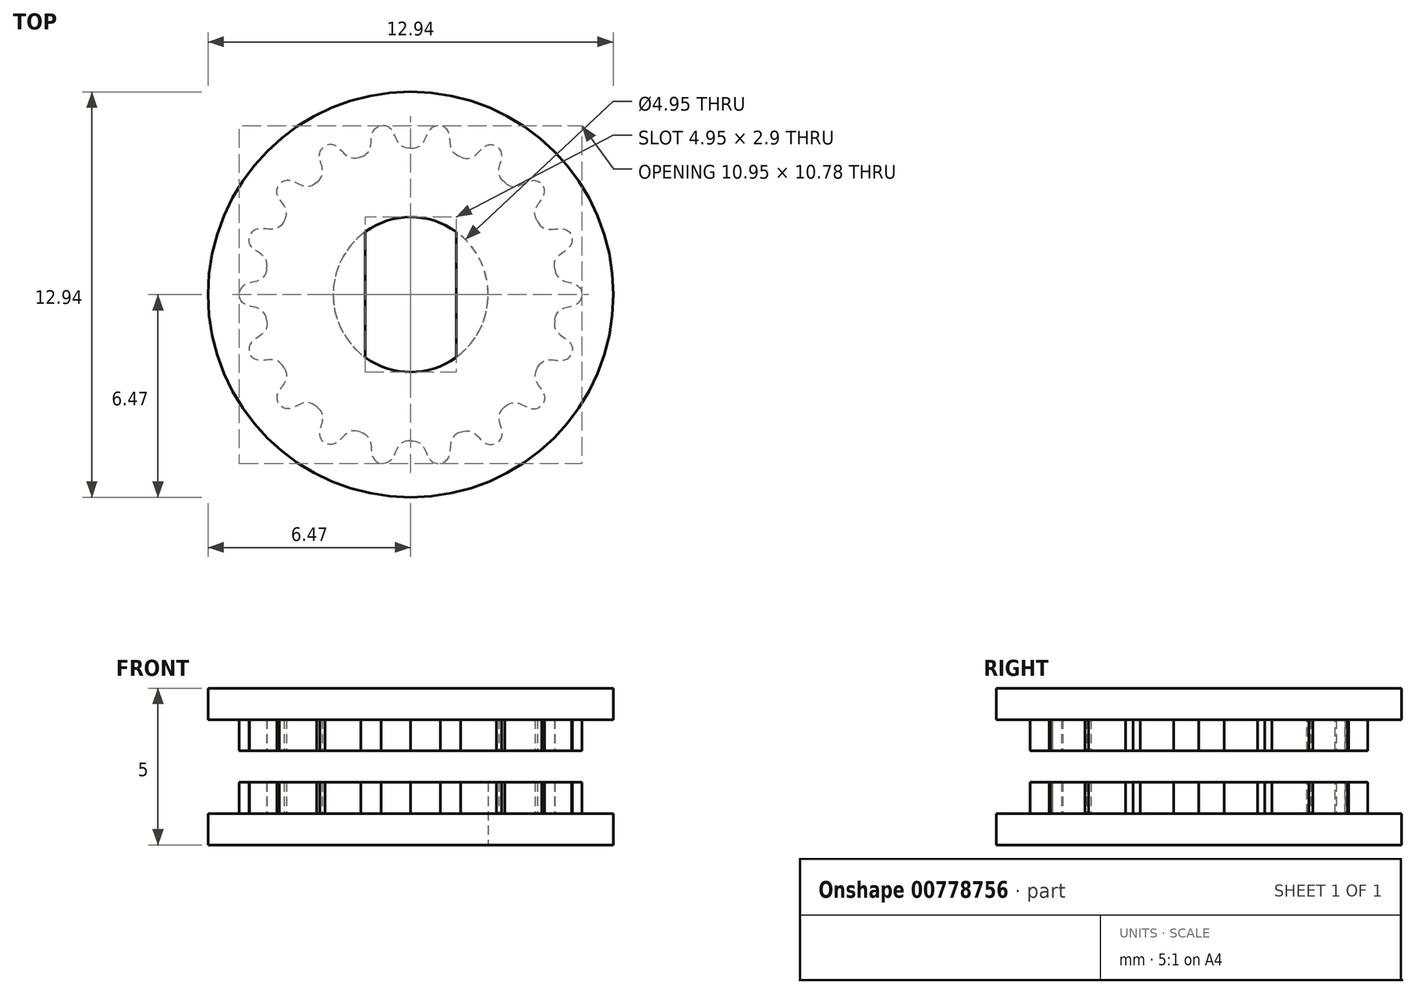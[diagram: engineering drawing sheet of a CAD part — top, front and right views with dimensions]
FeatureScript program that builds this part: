
annotation { "Feature Type Name" : "Feature", "Feature Type Description" : "" }
export const myFeature = defineFeature(function(context is Context, id is Id, definition is map)
    precondition{}
    {
        {
            assignVariable(context, id + "F0", {"name" : "teeth", "anyValue" : 18});
        }
        {
            var Q0;
            Q0=qCreatedBy(makeId("Top.planeOp"),FACE);
            var sketch = newSketch(context, id + "F1", { "sketchPlane" : qUnion([Q0])});
            skCircle(sketch, "E0", {"center": v(0, 0) * mm, "radius": 5.47 * mm, "construction": true});
            skLineSegment(sketch, "E1", {"start": v(0, 0) * mm, "end": v(0, 5.47) * mm, "construction": true});
            skLineSegment(sketch, "E2", {"start": v(0, 0) * mm, "end": v(0.95, 5.4) * mm, "construction": true});
            skArc(sketch, "E3", {"start": v(0.81, 4.6) * mm, "mid": v(0.4, 4.66) * mm, "end": v(0, 4.67) * mm, "construction": true});
            skLineSegment(sketch, "E4", {"start": v(0.61, 5.44) * mm, "end": v(0, 1.98) * mm, "construction": true});
            skFitSpline(sketch, "E5", {"points": [v(0, 4.67) * mm, v(0.57, 5.2) * mm, v(0.95, 5.4) * mm], "startDerivative": vector(2.16, -0.1) * mm, "endDerivative": vector(1.18, -0.19) * mm});
            skFitSpline(sketch, "E6.MirrorCS", {"points": [v(0, 4.67) * mm, v(-0.57, 5.2) * mm, v(-0.95, 5.4) * mm], "startDerivative": vector(-2.16, -0.1) * mm, "endDerivative": vector(-1.18, -0.19) * mm});
            skArc(sketch, "E7", {"start": v(0.95, 5.4) * mm, "mid": v(0, 5.47) * mm, "end": v(-0.95, 5.4) * mm});
            skLineSegment(sketch, "E8", {"start": v(-0.95, 5.4) * mm, "end": v(-1.12, 6.37) * mm});
            skArc(sketch, "E9", {"start": v(1.12, 6.37) * mm, "mid": v(0, 6.47) * mm, "end": v(-1.12, 6.37) * mm});
            skLineSegment(sketch, "E10", {"start": v(1.12, 6.37) * mm, "end": v(0.95, 5.4) * mm});
            skSolve(sketch);
        }
        {
            var Q0;
            Q0=qCreatedBy(makeId("Top.planeOp"),FACE);
            var sketch = newSketch(context, id + "F2", { "sketchPlane" : qUnion([Q0])});
            skCircle(sketch, "E11", {"center": v(0, 0) * mm, "radius": 6.47 * mm});
            skCircle(sketch, "E12", {"center": v(0, 0) * mm, "radius": 2.48 * mm});
            skLineSegment(sketch, "E13", {"start": v(-1.45, 2) * mm, "end": v(-1.45, -2) * mm});
            skLineSegment(sketch, "E14", {"start": v(1.45, 2) * mm, "end": v(1.45, -2) * mm});
            skSolve(sketch);
        }
        {
            var Q0;
            Q0=makeQuery(id+"F2.imprint","IMPRINT",FACE,{"disambiguationData":[TD([[makeQuery(id+"F2.imprint","IMPRINT",EDGE,{"derivedFrom":sQuery(id+"F2.wireOp",EDGE,"E11")}),1.0]])]});
            var Q1;
            {var subQ0=sQuery(id+"F2.wireOp",EDGE,"E13");Q1=makeQuery(id+"F2.imprint","IMPRINT",FACE,{"disambiguationData":[TD([[makeQuery(id+"F2.imprint","IMPRINT",EDGE,{"derivedFrom":subQ0}),-1.0]])]});}
            var Q2;
            {var subQ0=sQuery(id+"F2.wireOp",EDGE,"E14");Q2=makeQuery(id+"F2.imprint","IMPRINT",FACE,{"disambiguationData":[TD([[makeQuery(id+"F2.imprint","IMPRINT",EDGE,{"derivedFrom":subQ0}),1.0]])]});}
            extrude(context, id + "F3", {"entities" : qUnion([Q0, Q1, Q2]), "depth" : 2.5 * mm, "offsetDistance" : 25 * mm});
        }
        {
            var Q0;
            Q0=makeQuery(id+"F2.imprint","IMPRINT",FACE,{"disambiguationData":[TD([[makeQuery(id+"F2.imprint","IMPRINT",EDGE,{"derivedFrom":sQuery(id+"F2.wireOp",EDGE,"E11")}),1.0]])]});
            extrude(context, id + "F4", {"entities" : qUnion([Q0]), "operationType" : NewBodyOperationType.ADD, "oppositeDirection" : true, "depth" : 2.5 * mm, "offsetDistance" : 25 * mm});
        }
        {
            var Q0;
            Q0=qSketchRegion(id+"F1",true);
            extrude(context, id + "F5", {"entities" : qUnion([Q0]), "endBound" : BoundingType.SYMMETRIC, "depth" : 3 * mm, "offsetDistance" : 25 * mm});
        }
        {
            var Q0;
            Q0=makeQuery(id+"F5.opExtrude","SWEPT_BODY",BODY,{"disambiguationData":[OSD([sQuery(id+"F1.wireOp",EDGE,"E5"),sQuery(id+"F1.wireOp",EDGE,"E6.MirrorCS"),sQuery(id+"F1.wireOp",EDGE,"E7")])]});
            var Q1;
            Q1=sQuery(id+"F1.wireOp",EDGE,"E0");
            circularPattern(context, id + "F6", {"operationType" : NewBodyOperationType.REMOVE, "entities" : qUnion([Q0]), "axis" : qUnion([Q1]), "angle" : 360 * degree, "instanceCount" : getVariable(context, 'teeth'), "equalSpace" : true});
        }
        {
            var Q0;
            Q0=qSketchRegion(id+"F2",true);
            var Q1;
            {var subQ0=sQuery(id+"F2.wireOp",EDGE,"E14");Q1=makeQuery(id+"F2.imprint","IMPRINT",FACE,{"disambiguationData":[TD([[makeQuery(id+"F2.imprint","IMPRINT",EDGE,{"derivedFrom":subQ0}),1.0]])]});}
            var Q2;
            {var subQ0=sQuery(id+"F2.wireOp",EDGE,"E13");Q2=makeQuery(id+"F2.imprint","IMPRINT",FACE,{"disambiguationData":[TD([[makeQuery(id+"F2.imprint","IMPRINT",EDGE,{"derivedFrom":subQ0}),1.0]])]});}
            var Q3;
            {var subQ0=sQuery(id+"F2.wireOp",EDGE,"E13");Q3=makeQuery(id+"F2.imprint","IMPRINT",FACE,{"disambiguationData":[TD([[makeQuery(id+"F2.imprint","IMPRINT",EDGE,{"derivedFrom":subQ0}),-1.0]])]});}
            extrude(context, id + "F7", {"entities" : qUnion([Q0, Q1, Q2, Q3]), "operationType" : NewBodyOperationType.REMOVE, "endBound" : BoundingType.SYMMETRIC, "oppositeDirection" : true, "depth" : 1 * mm, "offsetDistance" : 25 * mm});
        }
        {
            var Q0;
            Q0=makeQuery(id+"F7.boolean.opBoolean","SPLIT",BODY,{"disambiguationData":[OD(0.0)],"derivedFrom":makeQuery(id+"F3.opExtrude","SWEPT_BODY",BODY,{"disambiguationData":[OSD([sQuery(id+"F2.wireOp",EDGE,"E11"),sQuery(id+"F2.wireOp",EDGE,"E12"),sQuery(id+"F2.wireOp",EDGE,"E13"),sQuery(id+"F2.wireOp",EDGE,"E14")])]})});
            transform(context, id + "F8", {"entities" : qUnion([Q0]), "transformType" : TransformType.TRANSLATION_3D, "dx" : 0 * mm, "dy" : 0 * mm, "dz" : -10 * mm, "makeCopy" : false});
        }
    });
